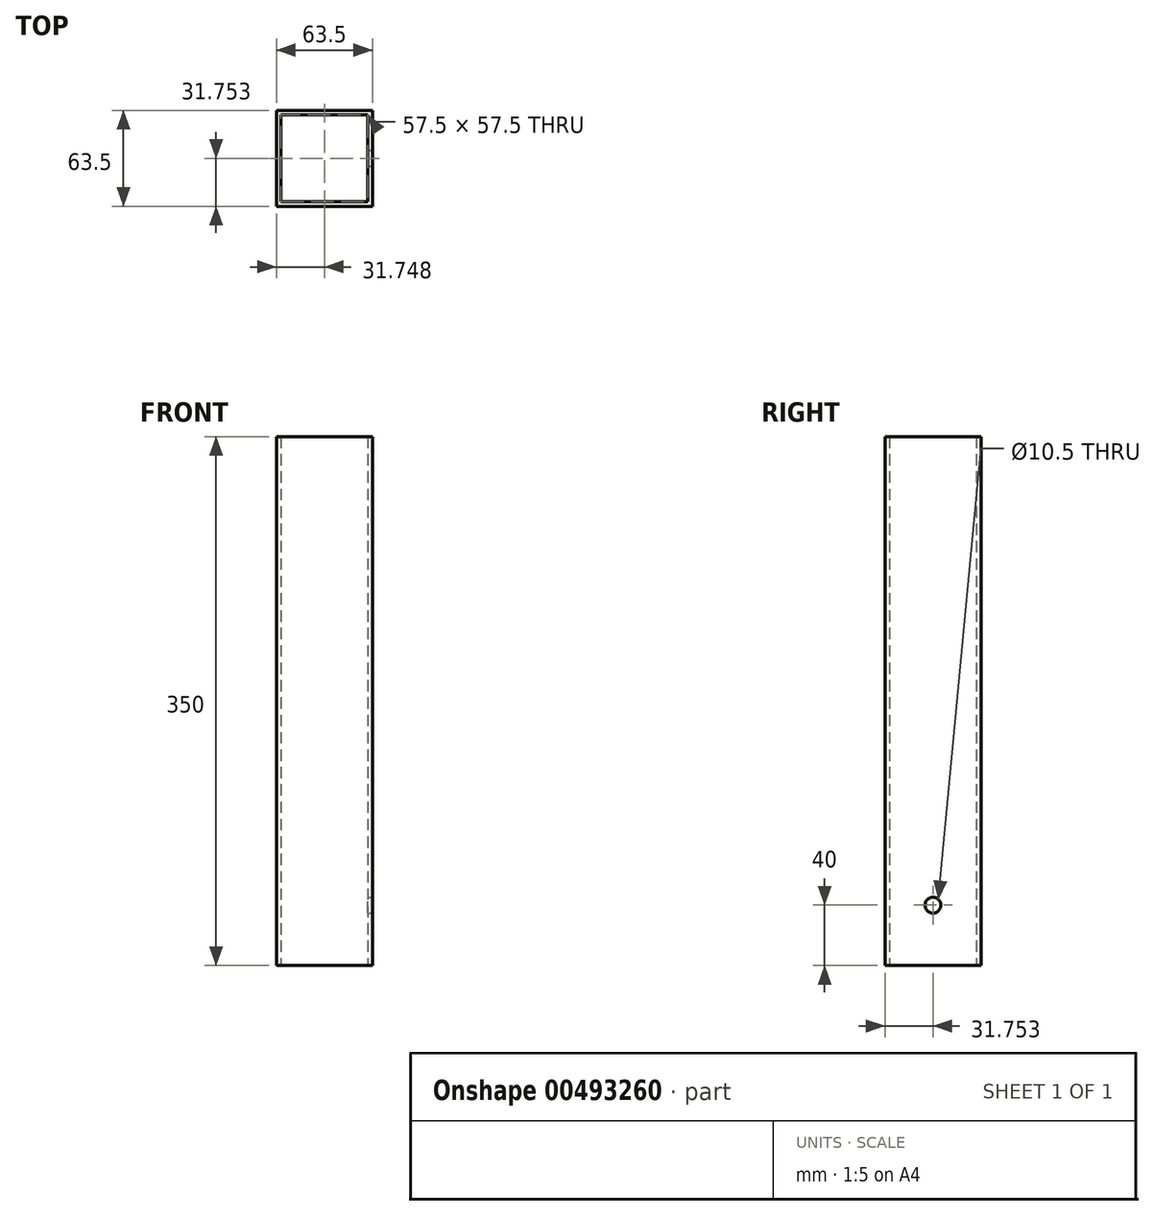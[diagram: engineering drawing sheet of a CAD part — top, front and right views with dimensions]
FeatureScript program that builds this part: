
annotation { "Feature Type Name" : "Feature", "Feature Type Description" : "" }
export const myFeature = defineFeature(function(context is Context, id is Id, definition is map)
    precondition{}
    {
        {
            var Q0;
            Q0=qCreatedBy(makeId("Top.planeOp"),FACE);
            var sketch = newSketch(context, id + "F0", { "sketchPlane" : qUnion([Q0])});
            skLineSegment(sketch, "E0.bottom", {"start": v(-26.21, 26.23) * mm, "end": v(31.29, 26.23) * mm});
            skLineSegment(sketch, "E0.top", {"start": v(-26.21, -31.27) * mm, "end": v(31.29, -31.27) * mm});
            skLineSegment(sketch, "E0.left", {"start": v(-26.21, 26.23) * mm, "end": v(-26.21, -31.27) * mm});
            skLineSegment(sketch, "E0.right", {"start": v(31.29, 26.23) * mm, "end": v(31.29, -31.27) * mm});
            skLineSegment(sketch, "E1.bottom", {"start": v(-29.21, 29.23) * mm, "end": v(34.29, 29.23) * mm});
            skLineSegment(sketch, "E1.top", {"start": v(-29.21, -34.27) * mm, "end": v(34.29, -34.27) * mm});
            skLineSegment(sketch, "E1.left", {"start": v(-29.21, 29.23) * mm, "end": v(-29.21, -34.27) * mm});
            skLineSegment(sketch, "E1.right", {"start": v(34.29, 29.23) * mm, "end": v(34.29, -34.27) * mm});
            skSolve(sketch);
        }
        {
            var Q0;
            Q0 = qSketchRegion(id + "F0", true);
            extrude(context, id + "F1", {"entities" : qUnion([Q0]), "depth" : 350 * mm});
        }
        {
            var Q0;
            Q0=makeQuery(id+"F1.opExtrude","SWEPT_FACE",FACE,{"disambiguationData":[OSD([sQuery(id+"F0.wireOp",EDGE,"E1.right")])]});
            var sketch = newSketch(context, id + "F2", { "sketchPlane" : qUnion([Q0])});
            skCircle(sketch, "E2", {"center": v(-2.52, 40) * mm, "radius": 5.25 * mm});
            skSolve(sketch);
        }
        {
            var Q0;
            Q0 = qSketchRegion(id + "F2", true);
            extrude(context, id + "F3", {"entities" : qUnion([Q0]), "operationType" : NewBodyOperationType.REMOVE, "oppositeDirection" : true, "depth" : 25 * mm});
        }
    });
